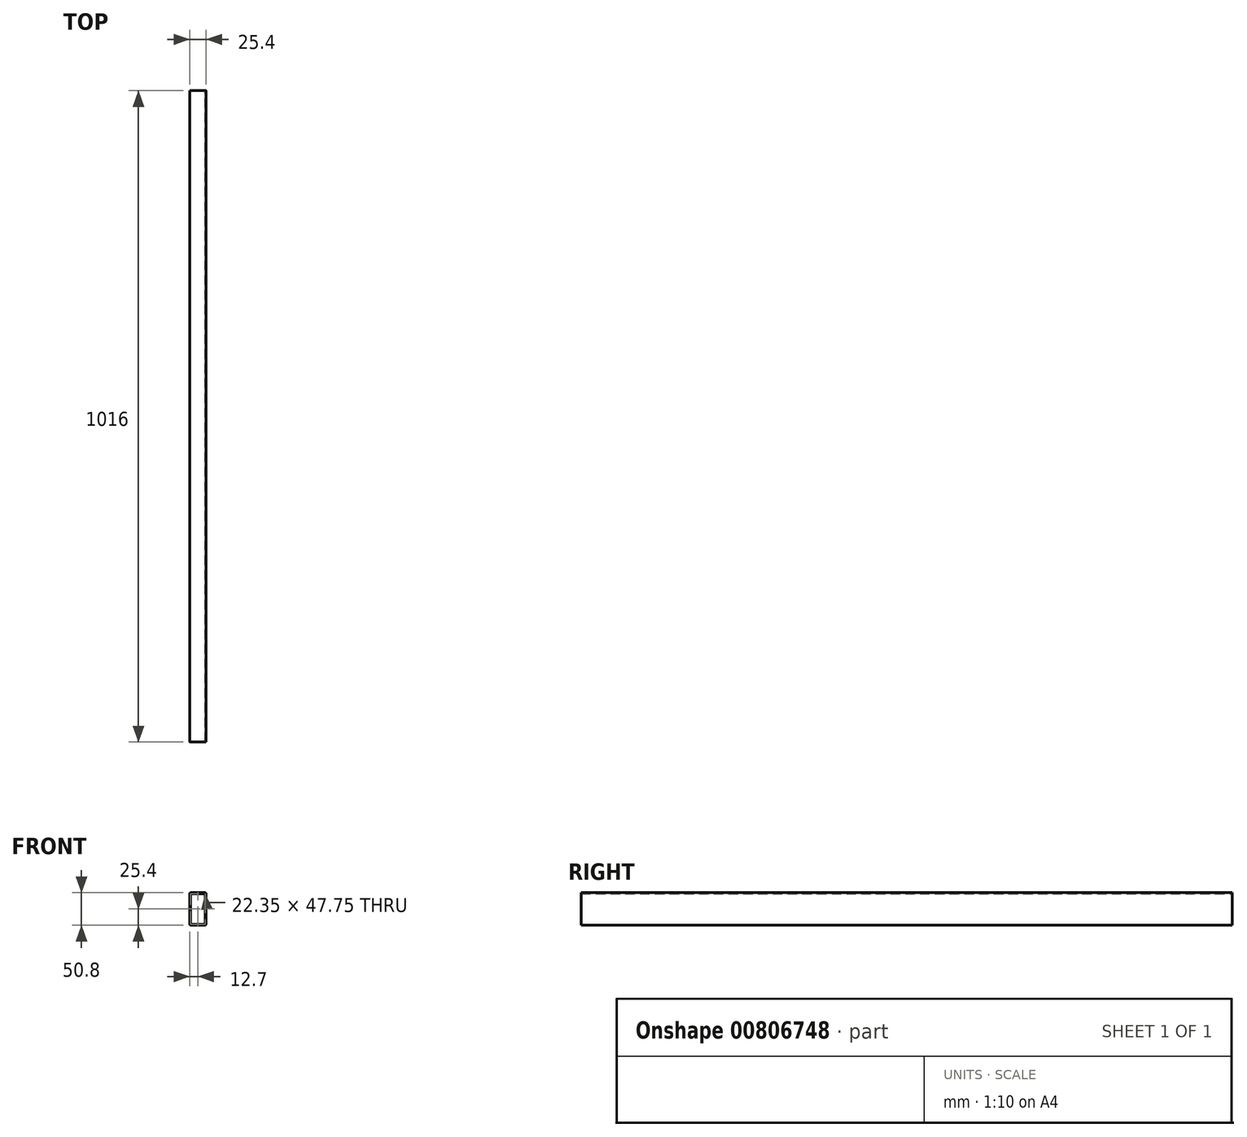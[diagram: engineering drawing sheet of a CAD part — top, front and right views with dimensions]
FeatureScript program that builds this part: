
annotation { "Feature Type Name" : "Feature", "Feature Type Description" : "" }
export const myFeature = defineFeature(function(context is Context, id is Id, definition is map)
    precondition{}
    {
        {
            var Q0;
            Q0=qCreatedBy(makeId("Front.planeOp"),FACE);
            var sketch = newSketch(context, id + "F0", { "sketchPlane" : qUnion([Q0])});
            skLineSegment(sketch, "E0.bottom", {"start": v(1.52, 0) * mm, "end": v(23.88, 0) * mm});
            skLineSegment(sketch, "E0.top", {"start": v(1.52, 50.8) * mm, "end": v(23.88, 50.8) * mm});
            skLineSegment(sketch, "E0.left", {"start": v(0, 1.52) * mm, "end": v(0, 49.28) * mm});
            skLineSegment(sketch, "E0.right", {"start": v(25.4, 1.52) * mm, "end": v(25.4, 49.28) * mm});
            skPoint(sketch, "E1.visualSharp", {"position": v(0, 50.8) * mm});
            skArc(sketch, "E1.filletArc", {"start": v(1.52, 50.8) * mm, "mid": v(0.45, 50.35) * mm, "end": v(0, 49.28) * mm});
            skPoint(sketch, "E2.visualSharp", {"position": v(25.4, 50.8) * mm});
            skArc(sketch, "E2.filletArc", {"start": v(25.4, 49.28) * mm, "mid": v(24.95, 50.35) * mm, "end": v(23.88, 50.8) * mm});
            skPoint(sketch, "E3.visualSharp", {"position": v(25.4, 0) * mm});
            skArc(sketch, "E3.filletArc", {"start": v(23.88, 0) * mm, "mid": v(24.95, 0.45) * mm, "end": v(25.4, 1.52) * mm});
            skPoint(sketch, "E4.visualSharp", {"position": v(0, 0) * mm});
            skArc(sketch, "E4.filletArc", {"start": v(0, 1.52) * mm, "mid": v(0.45, 0.45) * mm, "end": v(1.52, 0) * mm});
            skLineSegment(sketch, "E5.0", {"start": v(23.88, 1.52) * mm, "end": v(23.88, 49.28) * mm});
            skLineSegment(sketch, "E5.1", {"start": v(1.52, 1.52) * mm, "end": v(23.88, 1.52) * mm});
            skLineSegment(sketch, "E5.2", {"start": v(1.52, 1.52) * mm, "end": v(1.52, 49.28) * mm});
            skLineSegment(sketch, "E5.3", {"start": v(1.52, 49.28) * mm, "end": v(23.88, 49.28) * mm});
            skSolve(sketch);
        }
        {
            var Q0;
            Q0 = qSketchRegion(id + "F0", true);
            extrude(context, id + "F1", {"entities" : qUnion([Q0]), "depth" : 1016 * mm, "offsetDistance" : 25.4 * mm});
        }
    });
